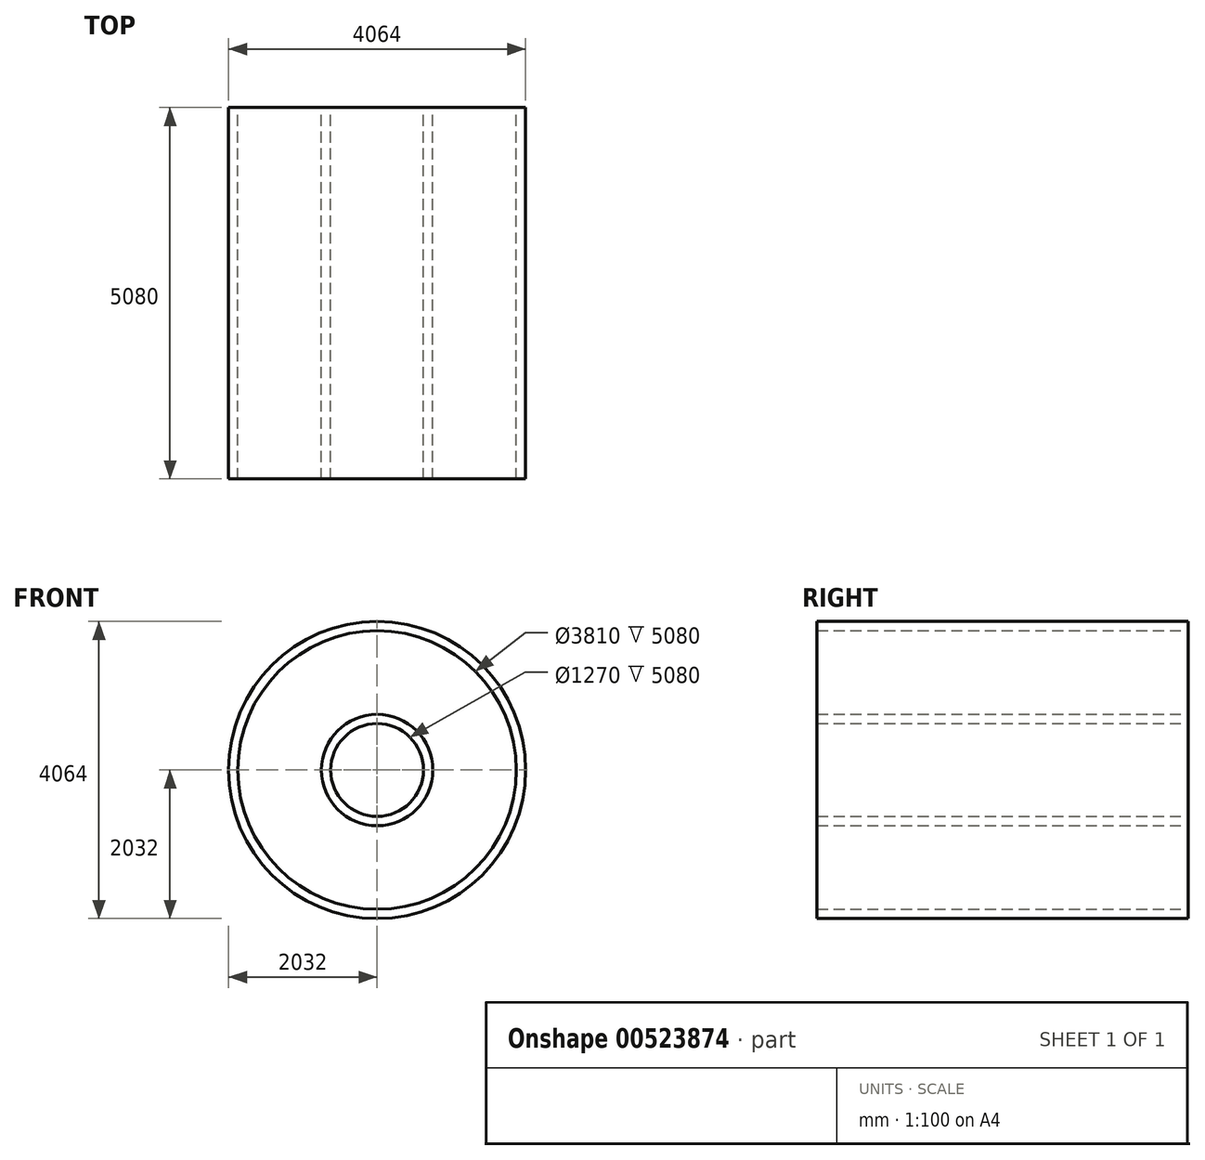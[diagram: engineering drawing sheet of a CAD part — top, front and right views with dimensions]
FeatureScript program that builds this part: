
annotation { "Feature Type Name" : "Feature", "Feature Type Description" : "" }
export const myFeature = defineFeature(function(context is Context, id is Id, definition is map)
    precondition{}
    {
        {
            var Q0;
            Q0=qCreatedBy(makeId("Front.planeOp"),FACE);
            var sketch = newSketch(context, id + "F0", { "sketchPlane" : qUnion([Q0])});
            skCircle(sketch, "E0", {"center": v(0, 0) * mm, "radius": 1905 * mm});
            skCircle(sketch, "E1", {"center": v(0, 0) * mm, "radius": 2032 * mm});
            skCircle(sketch, "E2", {"center": v(0, 0) * mm, "radius": 762 * mm});
            skCircle(sketch, "E3", {"center": v(0, 0) * mm, "radius": 635 * mm});
            skSolve(sketch);
        }
        {
            var Q0;
            Q0=makeQuery(id+"F0.imprint","IMPRINT",FACE,{"disambiguationData":[TD([[makeQuery(id+"F0.imprint","IMPRINT",EDGE,{"derivedFrom":sQuery(id+"F0.wireOp",EDGE,"E0")}),-1.0]])]});
            var Q1;
            Q1=makeQuery(id+"F0.imprint","IMPRINT",FACE,{"disambiguationData":[TD([[makeQuery(id+"F0.imprint","IMPRINT",EDGE,{"derivedFrom":sQuery(id+"F0.wireOp",EDGE,"E2")}),1.0]])]});
            extrude(context, id + "F1", {"entities" : qUnion([Q0, Q1]), "depth" : 5080 * mm, "offsetDistance" : 25.4 * mm});
        }
        {
            var Q0;
            Q0=qCreatedBy(makeId("Right.planeOp"),FACE);
            cPlane(context, id + "F2", {"entities" : qUnion([Q0]), "cplaneType" : CPlaneType.OFFSET, "offset" : 7620 * mm, "oppositeDirection" : true, "width" : 152.4 * mm, "height" : 152.4 * mm});
        }
    });
